# Revit family: Valve-Angle-Cla_Val-B50AE_01-Threaded-SI--
name_source: partatom
category: Pipe Accessories
units: mm (PartAtom-declared; Revit-internal decimal feet)

## family parameters
Always vertical = Yes
Cut with Voids When Loaded = No
Part Type = Valve - Breaks Into
Round Connector Dimension = Use Diameter
Shared = No
Work Plane-Based = No

## types (1)
- ERROR_LOAD TYPE CATALOG
    Assembly Code = D2090
    Body Material = Metal - CLA-VAL - Ductile Iron - Red
    CV (liters per second) = 6
    Connection Axis to Primary End = 31 mm  [stored 0.101706 ft]
    Connection Axis to Secondary End = 66 mm
    Connection Axis to Side Ports = 37 mm
    Connection Axis to Upper Cover Flange = 68 mm  [stored 0.223097 ft]
    Connection Axis to Valve Top = 140 mm  [stored 0.459318 ft]
    Connection Radius = 16 mm
    Connection Size = 32 mm
    Connection Type = Threaded 1-1/4" BSP
    Cover Port Center Offset = 30 mm  [stored 0.0984252 ft]
    Cover Upper Flange Radius = 73 mm  [stored 0.239501 ft]
    Default Elevation = 0 mm  [stored 0 ft]
    Description = Pressure Relief & Pressure Sustaining Valve
    ENGworks Global = http://www.ENGworksGlobal.com
    Flow Configuration = In/Out
    Four Port Cover = No
    Isometric Symbol Radius = 28 mm
    Isometric Symbol Stem Length = 31 mm  [stored 0.101706 ft]
    Isometric Tick Size = 55 mm
    K Coefficient = 0.358053
    K Coefficient Table = Angle Valve Threaded
    Kv Coefficient = 82.22512
    Loss Method = K Coefficient
    Manufacturer = Cla-Val
    Maximum Flow Rate = 6.000 L/s
    Maximum Flow Rate Value = 6
    Maximum Operating Temperature = 65 °C
    Maximum Working Pressure = 16 bar
    Minimum Flow Rate = 0.000 L/s
    Minimum Flow Rate Value = 0
    Minimum Operating Temperature = 0 °C
    Model = B50AE-01
    Pilot System Offset = 87 mm  [stored 0.285433 ft]
    Pilot System Pipe Diameter = 10 mm
    Pilot System Pipe Radius = 5 mm
    Pipe Angle Offset = 27 mm
    Plan Symbol Radius = 13 mm
    Plan Symbol Stem Length = 22 mm
    Plan Tick Size = 25 mm  [stored 0.082021 ft]
    Product Page URL = https://www.cla-val.co.uk
    Series = Pressure Relief & Pressure Sustaining Valve
    Side Ports Horizontal Offset = 51 mm  [stored 0.167323 ft]
    Standards = ASTM A536, B16.42
    Threaded End Length = 18 mm
    Top Port Vertical Offset = 18 mm
    Two Port Cover = Yes
    URL = https://www.cla-val.co.uk
    Unit Weight = 13 kgf
    Unit Weight Value = 13
    Version = 1
    X Pilot System Offset = 252 mm
    Y Pilot System Offset = 145 mm  [stored 0.475722 ft]
    Z Pilot System Offset = 150 mm  [stored 0.492126 ft]

note: [stored X ft] marks values corroborated as IEEE doubles in the binary element streams (Revit-internal decimal feet)

## geometry (parser evidence)
native form markers: Sweep x6
no freeform markers — native parametric forms only
